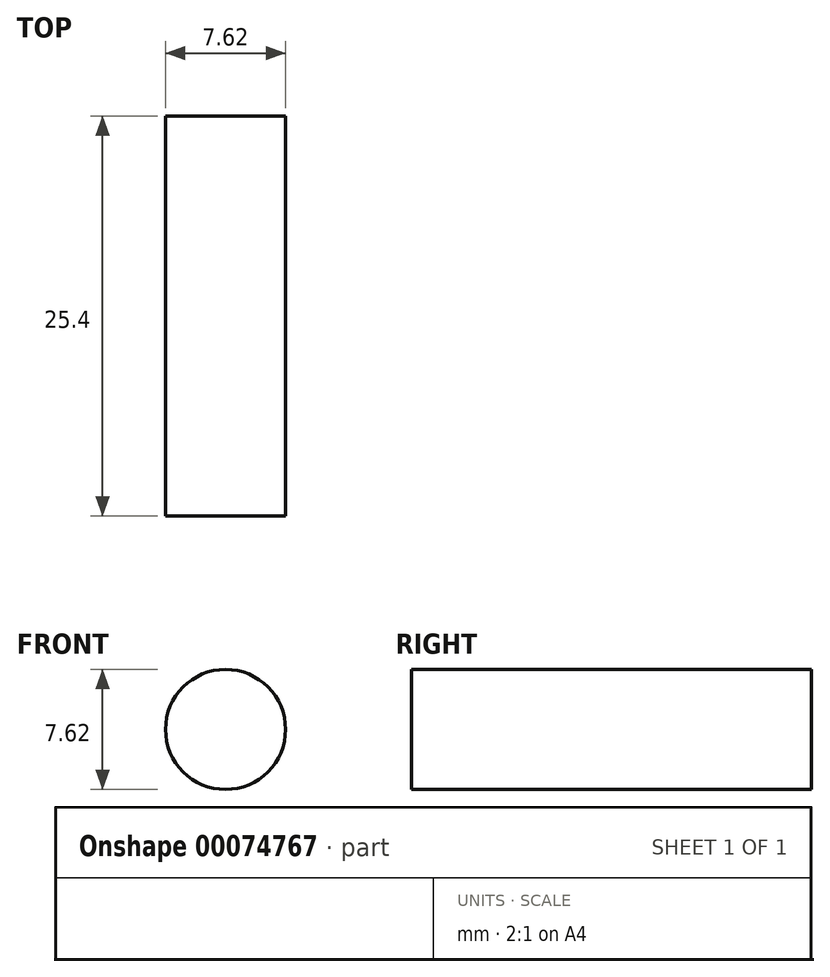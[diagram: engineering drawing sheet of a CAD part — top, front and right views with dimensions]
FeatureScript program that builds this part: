
annotation { "Feature Type Name" : "Feature", "Feature Type Description" : "" }
export const myFeature = defineFeature(function(context is Context, id is Id, definition is map)
    precondition{}
    {
        {
            var Q0;
            Q0=qCreatedBy(makeId("Front.planeOp"),FACE);
            var sketch = newSketch(context, id + "F0", { "sketchPlane" : qUnion([Q0])});
            skCircle(sketch, "E0", {"center": v(0, 0) * mm, "radius": 3.81 * mm});
            skSolve(sketch);
        }
        {
            var Q0;
            Q0=makeQuery(id+"F0.imprint","IMPRINT",FACE,{"disambiguationData":[TD([[makeQuery(id+"F0.imprint","IMPRINT",EDGE,{"derivedFrom":sQuery(id+"F0.wireOp",EDGE,"E0")}),1.0]])]});
            extrude(context, id + "F1", {"entities" : qUnion([Q0]), "depth" : 25.4 * mm});
        }
    });
